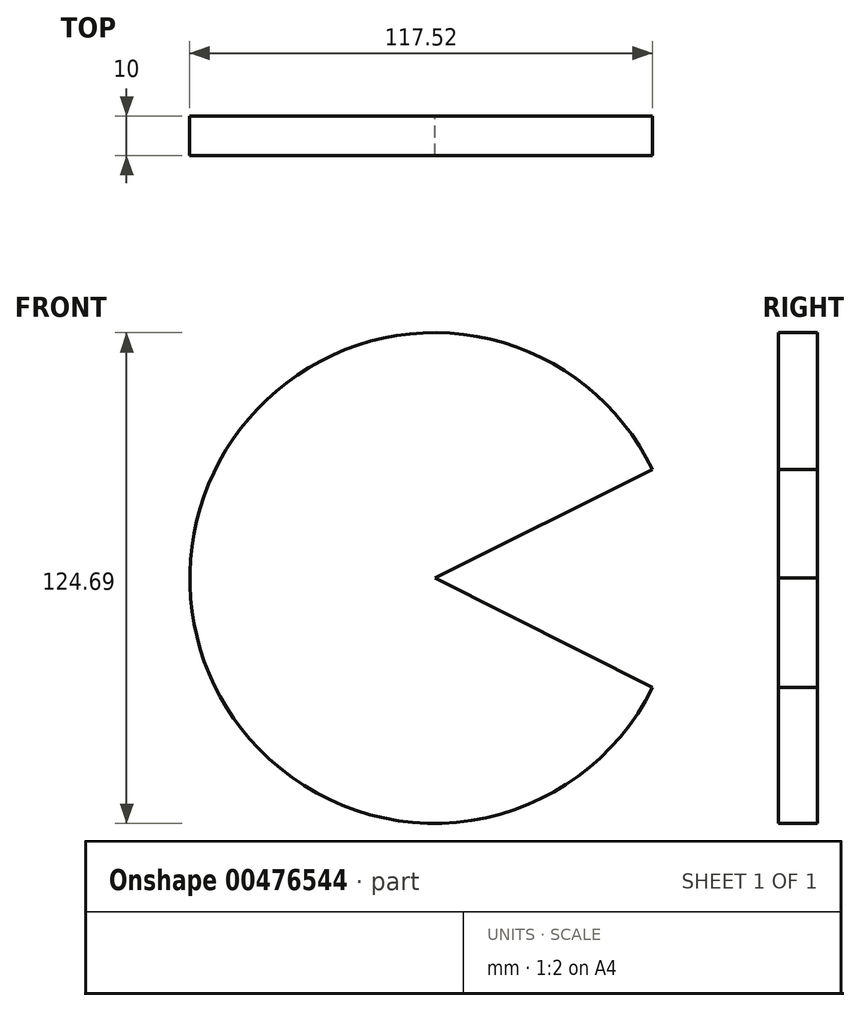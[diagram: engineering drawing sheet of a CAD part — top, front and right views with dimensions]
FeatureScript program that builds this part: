
annotation { "Feature Type Name" : "Feature", "Feature Type Description" : "" }
export const myFeature = defineFeature(function(context is Context, id is Id, definition is map)
    precondition{}
    {
        {
            var Q0;
            Q0=qCreatedBy(makeId("Front.planeOp"),FACE);
            var sketch = newSketch(context, id + "F0", { "sketchPlane" : qUnion([Q0])});
            skLineSegment(sketch, "E0", {"start": v(62.52, 30.81) * mm, "end": v(7.3, 3.27) * mm});
            skLineSegment(sketch, "E1", {"start": v(7.3, 3.27) * mm, "end": v(62.52, -24.56) * mm});
            skArc(sketch, "E2", {"start": v(62.52, 30.81) * mm, "mid": v(21.33, 63.97) * mm, "end": v(-30.37, 52.85) * mm});
            skArc(sketch, "E3", {"start": v(-30.37, 52.85) * mm, "mid": v(-54.82, 8) * mm, "end": v(-37.51, -40.04) * mm});
            skArc(sketch, "E4", {"start": v(-37.51, -40.04) * mm, "mid": v(16.53, -58.33) * mm, "end": v(62.52, -24.56) * mm});
            skSolve(sketch);
        }
        {
            var Q0;
            Q0=makeQuery(id+"F0.imprint","IMPRINT",FACE,{"disambiguationData":[TD([[makeQuery(id+"F0.imprint","IMPRINT",EDGE,{"derivedFrom":sQuery(id+"F0.wireOp",EDGE,"E0")}),-1.0]])]});
            extrude(context, id + "F1", {"entities" : qUnion([Q0]), "depth" : 10 * mm});
        }
    });
